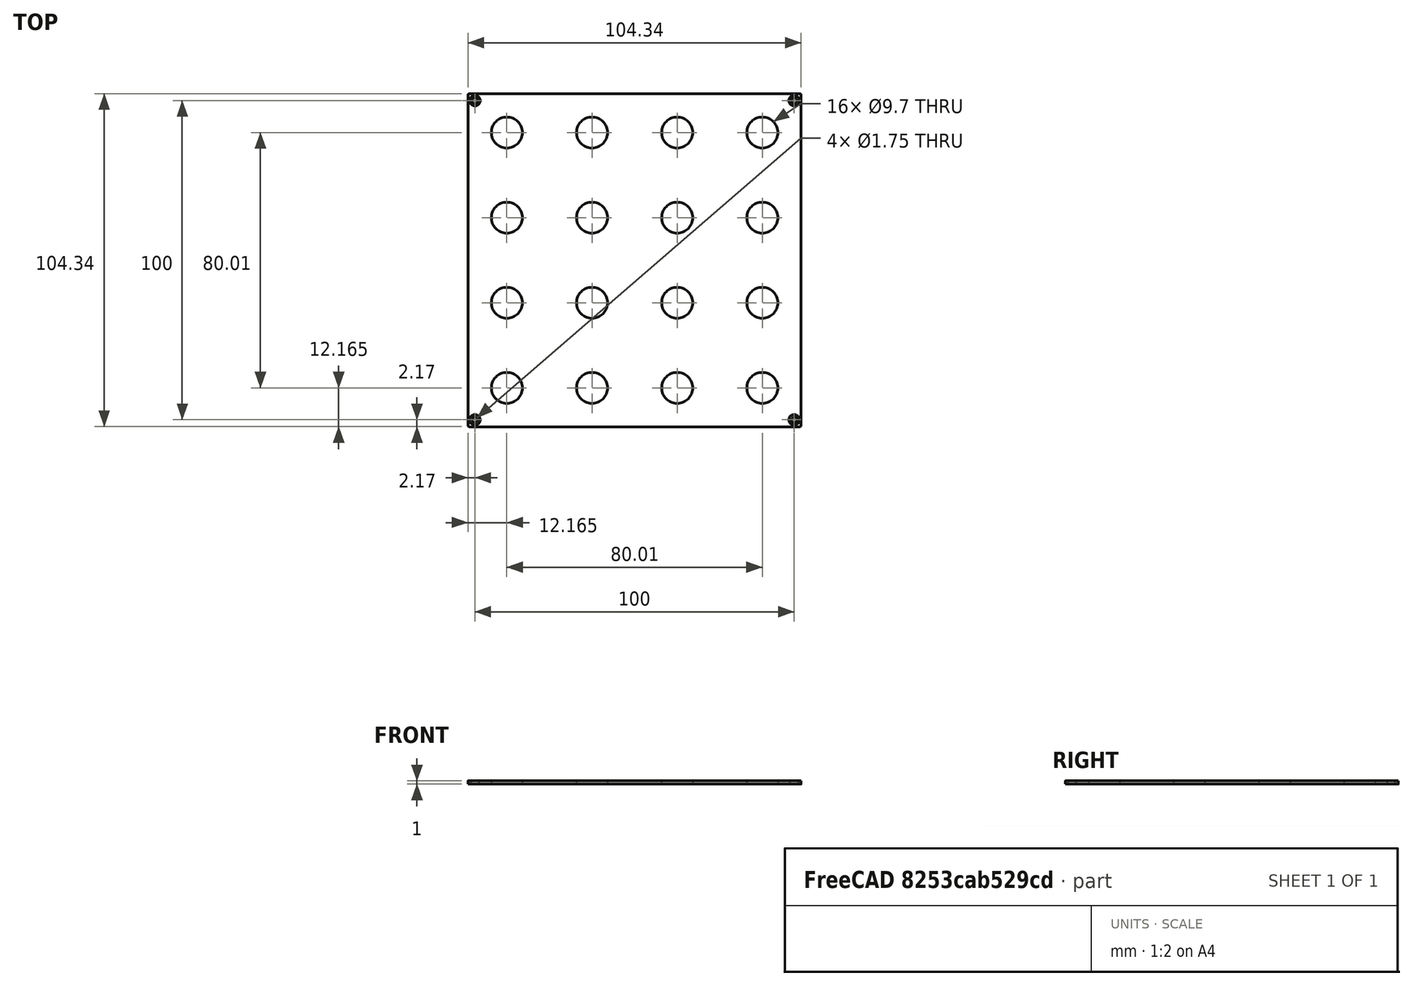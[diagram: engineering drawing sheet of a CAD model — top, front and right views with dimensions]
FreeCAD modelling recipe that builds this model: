
FCSTD DOCUMENT  (FreeCAD 0.21R33668 +26 (Git))
Label: FRONTPANEL-SHEET-BU16_wo_lightpipe
License: All rights reserved
LicenseURL: https://en.wikipedia.org/wiki/All_rights_reserved
objects: TechDraw::DrawViewBalloon×10, TechDraw::DrawViewDimension×8, Sketcher::SketchObject×6, TechDraw::DrawViewPart×5, TechDraw::DrawViewAnnotation×3, TechDraw::DrawSVGTemplate×2, PartDesign::Hole×2, PartDesign::Body×2, TechDraw::DrawPage×2, Spreadsheet::Sheet×1, PartDesign::Pad×1, PartDesign::Pocket×1, PartDesign::FeatureBase×1, TechDraw::DrawHatch×1, TechDraw::DrawComplexSection×1
note: 28 computed .brp shape members not serialized (recipe doc carries the construction recipe); baked Part::Feature solids carry a one-line shape summary decoded from their .brp

FEATURE [TechDraw::DrawSVGTemplate] Template003
  EditableTexts = COLOR=Anodized matte black - RAL code: 9004; CreationDate=2023/12/05; E.G.APPROVED=APPROVED; FC-Scale=1:1; FC-Title=BU16 - top cover; IntechStudioLtd.=Intech Studio Ltd.; MATERIAL=Aluminum 5052-H32; REV=02; STANDARD=ISO 2768 - m
  Height = 297
  Orientation = 1
  Template = <userpath>/Desktop/A3_LandscapeTD_MODIFIED.svg
  Width = 420
FEATURE [Spreadsheet::Sheet] Spreadsheet  label="dim"
  cells = A1='panel_length; B1(panel_length)=104.35; A2='panel_thickness; B2(panel_thickness)=1; A3='panel_radius; B3(panel_radius)==(104.35 - 103.6) / 2; A5='corner_drill_dist; B5(corner_drill_dist)=100; A6='corner_drill_dia; B6(corner_drill_dia)=1.75; A7='corner_drill_countersink; B7(corner_drill_countersink)=3.3; A9='undercut_width; B9(undercut_width)=1; A10='undercut_length; B10(undercut_length)=90; A11='undercut_offset; B11(undercut_offset)=1; A12='undercut_depth; B12(undercut_depth)=0.8; A14='ui_raster; B14(ui_raster)=26.67; A16='light_drill_dia; B16(light_drill_dia)=3; D16='old 2.9; A17='light_bore_dia; B17(light_bore_dia)=3.45; C17='check; D17='old 3.30; E17='DEPRICATED; A18='light_bore_depth; B18(light_bore_depth)=0.4; C18='check; D18='old 0.40; E18='DEPRICATED; A20='pot_drill_dia; B20(pot_drill_dia)=9.7; C20='check; D20='old 6.20; A21='pot_led_dist; B21(pot_led_dist)=8.5; B22=0; A23='but_drill_dia; B23(but_drill_dia)=9.7; A24='but_led_dist; B24(but_led_dist)=8.5; A26='fad_cutout_width; B26(fad_cutout_width)=2; C26='check; D26='old 1.50; A27='fad_cutout_length; B27(fad_cutout_length)=36; A28='fad_led_dist; B28(fad_led_dist)=25; A30='enc_drill_dia; B30(enc_drill_dia)=9.7; C30='check; D30='old 6.20; A31='enc_led_dist; B31(enc_led_dist)=8.5; A33='longfad_cutout_width; B33(longfad_cutout_width)=2; A34='longfad_cutout_length; B34(longfad_cutout_length)=66; A36='panel_chamfer; B36(panel_chamfer)=0.2; C36='UPDATE DRAWING
FEATURE [Sketcher::SketchObject] Sketch006
  FullyConstrained = true
  MapMode = 5
  Support = -> [XY_Plane002]
  expr: Constraints[4] = <<dim>>.ui_raster
  expr: Constraints[84] = <<dim>>.but_led_dist
  sketch-geometry (34):
    g0: Circle CenterX=-40.005 CenterY=48.505 CenterZ=0 NormalX=0 NormalY=0 NormalZ=1 AngleXU=0 Radius=2
    g1: Circle CenterX=-13.335 CenterY=48.505 CenterZ=0 NormalX=0 NormalY=0 NormalZ=1 AngleXU=0 Radius=2
    g2: LineSegment StartX=-40.005 StartY=48.505 StartZ=0 EndX=-13.335 EndY=48.505 EndZ=0
    g3: Circle CenterX=13.335 CenterY=48.505 CenterZ=0 NormalX=0 NormalY=0 NormalZ=1 AngleXU=0 Radius=2
    g4: LineSegment StartX=-13.335 StartY=48.505 StartZ=0 EndX=13.335 EndY=48.505 EndZ=0
    g5: Circle CenterX=40.005 CenterY=48.505 CenterZ=0 NormalX=0 NormalY=0 NormalZ=1 AngleXU=0 Radius=2
    g6: LineSegment StartX=13.335 StartY=48.505 StartZ=0 EndX=40.005 EndY=48.505 EndZ=0
    g7: Circle CenterX=-40.005 CenterY=21.835 CenterZ=0 NormalX=0 NormalY=0 NormalZ=1 AngleXU=0 Radius=2
    g8: LineSegment StartX=-40.005 StartY=48.505 StartZ=0 EndX=-40.005 EndY=21.835 EndZ=0
    g9: Circle CenterX=-13.335 CenterY=21.835 CenterZ=0 NormalX=0 NormalY=0 NormalZ=1 AngleXU=0 Radius=2
    g10: LineSegment StartX=-40.005 StartY=21.835 StartZ=0 EndX=-13.335 EndY=21.835 EndZ=0
    g11: Circle CenterX=13.335 CenterY=21.835 CenterZ=0 NormalX=0 NormalY=0 NormalZ=1 AngleXU=0 Radius=2
    g12: LineSegment StartX=-13.335 StartY=21.835 StartZ=0 EndX=13.335 EndY=21.835 EndZ=0
    g13: Circle CenterX=40.005 CenterY=21.835 CenterZ=0 NormalX=0 NormalY=0 NormalZ=1 AngleXU=0 Radius=2
    g14: LineSegment StartX=13.335 StartY=21.835 StartZ=0 EndX=40.005 EndY=21.835 EndZ=0
    g15: Circle CenterX=-40.005 CenterY=-4.835 CenterZ=0 NormalX=0 NormalY=0 NormalZ=1 AngleXU=0 Radius=2
    g16: LineSegment StartX=-40.005 StartY=21.835 StartZ=0 EndX=-40.005 EndY=-4.835 EndZ=0
    g17: Circle CenterX=-13.335 CenterY=-4.835 CenterZ=0 NormalX=0 NormalY=0 NormalZ=1 AngleXU=0 Radius=2
    g18: LineSegment StartX=-40.005 StartY=-4.835 StartZ=0 EndX=-13.335 EndY=-4.835 EndZ=0
    g19: Circle CenterX=13.335 CenterY=-4.835 CenterZ=0 NormalX=0 NormalY=0 NormalZ=1 AngleXU=0 Radius=2
    g20: LineSegment StartX=-13.335 StartY=-4.835 StartZ=0 EndX=13.335 EndY=-4.835 EndZ=0
    g21: Circle CenterX=40.005 CenterY=-4.835 CenterZ=0 NormalX=0 NormalY=0 NormalZ=1 AngleXU=0 Radius=2
    g22: LineSegment StartX=13.335 StartY=-4.835 StartZ=0 EndX=40.005 EndY=-4.835 EndZ=0
    g23: Circle CenterX=-40.005 CenterY=-31.505 CenterZ=0 NormalX=0 NormalY=0 NormalZ=1 AngleXU=0 Radius=2
    g24: LineSegment StartX=-40.005 StartY=-4.835 StartZ=0 EndX=-40.005 EndY=-31.505 EndZ=0
    g25: Circle CenterX=-13.335 CenterY=-31.505 CenterZ=0 NormalX=0 NormalY=0 NormalZ=1 AngleXU=0 Radius=2
    g26: LineSegment StartX=-40.005 StartY=-31.505 StartZ=0 EndX=-13.335 EndY=-31.505 EndZ=0
    g27: Circle CenterX=13.335 CenterY=-31.505 CenterZ=0 NormalX=0 NormalY=0 NormalZ=1 AngleXU=0 Radius=2
    g28: LineSegment StartX=-13.335 StartY=-31.505 StartZ=0 EndX=13.335 EndY=-31.505 EndZ=0
    g29: Circle CenterX=40.005 CenterY=-31.505 CenterZ=0 NormalX=0 NormalY=0 NormalZ=1 AngleXU=0 Radius=2
    g30: LineSegment StartX=13.335 StartY=-31.505 StartZ=0 EndX=40.005 EndY=-31.505 EndZ=0
    g31: LineSegment StartX=-13.335 StartY=21.835 StartZ=0 EndX=-1.8e-15 EndY=8.5 EndZ=0
    g32: LineSegment StartX=-1.8e-15 StartY=8.5 StartZ=0 EndX=13.335 EndY=21.835 EndZ=0
    g33: LineSegment StartX=-1.8e-15 StartY=8.5 StartZ=0 EndX=-13.335 EndY=-4.835 EndZ=0
  constraints (85):
    c: Diameter(g0) = 4
    c: Diameter(g1) = 4
    c: Coincident(g0,g2)
    c: Coincident(g1,g2)
    c: Distance(g2) = 26.67
    c: Angle(g2) = 0
    c: Diameter(g3) = 4
    c: Coincident(g1,g4)
    c: Coincident(g3,g4)
    c: Equal(g2,g4)
    c: Parallel(g4,g2)
    c: Diameter(g5) = 4
    c: Coincident(g3,g6)
    c: Coincident(g5,g6)
    c: Equal(g2,g6)
    c: Parallel(g6,g2)
    c: Diameter(g7) = 4
    c: Coincident(g0,g8)
    c: Coincident(g7,g8)
    c: Equal(g8,g2)
    c: Perpendicular(g8,g2)
    c: Diameter(g9) = 4
    c: Coincident(g7,g10)
    c: Coincident(g9,g10)
    c: Equal(g2,g10)
    c: Parallel(g10,g2)
    c: Diameter(g11) = 4
    c: Coincident(g9,g12)
    c: Coincident(g11,g12)
    c: Equal(g2,g12)
    c: Parallel(g12,g2)
    c: Diameter(g13) = 4
    c: Coincident(g11,g14)
    c: Coincident(g13,g14)
    c: Equal(g2,g14)
    c: Parallel(g14,g2)
    c: Diameter(g15) = 4
    c: Coincident(g7,g16)
    c: Coincident(g15,g16)
    c: Equal(g8,g16)
    c: Perpendicular(g16,g2)
    c: Diameter(g17) = 4
    c: Coincident(g15,g18)
    c: Coincident(g17,g18)
    c: Equal(g2,g18)
    c: Parallel(g18,g2)
    c: Diameter(g19) = 4
    c: Coincident(g17,g20)
    c: Coincident(g19,g20)
    c: Equal(g2,g20)
    c: Parallel(g20,g2)
    c: Diameter(g21) = 4
    c: Coincident(g19,g22)
    c: Coincident(g21,g22)
    c: Equal(g2,g22)
    c: Parallel(g22,g2)
    c: Diameter(g23) = 4
    c: Coincident(g15,g24)
    c: Coincident(g23,g24)
    c: Equal(g8,g24)
    c: Perpendicular(g24,g2)
    c: Diameter(g25) = 4
    c: Coincident(g23,g26)
    c: Coincident(g25,g26)
    c: Equal(g2,g26)
    c: Parallel(g26,g2)
    c: Diameter(g27) = 4
    c: Coincident(g25,g28)
    c: Coincident(g27,g28)
    c: Equal(g2,g28)
    c: Parallel(g28,g2)
    c: Diameter(g29) = 4
    c: Coincident(g27,g30)
    c: Coincident(g29,g30)
    c: Equal(g2,g30)
    c: Parallel(g30,g2)
    c: Coincident(g31,g9)
    c: PointOnObject(g31,g-2)
    c: Coincident(g31,g32)
    c: Coincident(g32,g11)
    c: Coincident(g31,g33)
    c: Coincident(g33,g17)
    c: Equal(g33,g31)
    c: Equal(g31,g32)
    c: DistanceY(g-1,g31) = 8.5
FEATURE [Sketcher::SketchObject] Sketch005
  FullyConstrained = true
  MapMode = 5
  Support = -> [XY_Plane002]
  expr: Constraints[4] = <<dim>>.ui_raster
  sketch-geometry (34):
    g0: Circle CenterX=-40.005 CenterY=40.005 CenterZ=0 NormalX=0 NormalY=0 NormalZ=1 AngleXU=0 Radius=2
    g1: Circle CenterX=-13.335 CenterY=40.005 CenterZ=0 NormalX=0 NormalY=0 NormalZ=1 AngleXU=0 Radius=2
    g2: LineSegment StartX=-40.005 StartY=40.005 StartZ=0 EndX=-13.335 EndY=40.005 EndZ=0
    g3: Circle CenterX=13.335 CenterY=40.005 CenterZ=0 NormalX=0 NormalY=0 NormalZ=1 AngleXU=0 Radius=2
    g4: LineSegment StartX=-13.335 StartY=40.005 StartZ=0 EndX=13.335 EndY=40.005 EndZ=0
    g5: Circle CenterX=40.005 CenterY=40.005 CenterZ=0 NormalX=0 NormalY=0 NormalZ=1 AngleXU=0 Radius=2
    g6: LineSegment StartX=13.335 StartY=40.005 StartZ=0 EndX=40.005 EndY=40.005 EndZ=0
    g7: Circle CenterX=-40.005 CenterY=13.335 CenterZ=0 NormalX=0 NormalY=0 NormalZ=1 AngleXU=0 Radius=2
    g8: LineSegment StartX=-40.005 StartY=40.005 StartZ=0 EndX=-40.005 EndY=13.335 EndZ=0
    g9: Circle CenterX=-13.335 CenterY=13.335 CenterZ=0 NormalX=0 NormalY=0 NormalZ=1 AngleXU=0 Radius=2
    g10: LineSegment StartX=-40.005 StartY=13.335 StartZ=0 EndX=-13.335 EndY=13.335 EndZ=0
    g11: Circle CenterX=13.335 CenterY=13.335 CenterZ=0 NormalX=0 NormalY=0 NormalZ=1 AngleXU=0 Radius=2
    g12: LineSegment StartX=-13.335 StartY=13.335 StartZ=0 EndX=13.335 EndY=13.335 EndZ=0
    g13: Circle CenterX=40.005 CenterY=13.335 CenterZ=0 NormalX=0 NormalY=0 NormalZ=1 AngleXU=0 Radius=2
    g14: LineSegment StartX=13.335 StartY=13.335 StartZ=0 EndX=40.005 EndY=13.335 EndZ=0
    g15: Circle CenterX=-40.005 CenterY=-13.335 CenterZ=0 NormalX=0 NormalY=0 NormalZ=1 AngleXU=0 Radius=2
    g16: LineSegment StartX=-40.005 StartY=13.335 StartZ=0 EndX=-40.005 EndY=-13.335 EndZ=0
    g17: Circle CenterX=-13.335 CenterY=-13.335 CenterZ=0 NormalX=0 NormalY=0 NormalZ=1 AngleXU=0 Radius=2
    g18: LineSegment StartX=-40.005 StartY=-13.335 StartZ=0 EndX=-13.335 EndY=-13.335 EndZ=0
    g19: Circle CenterX=13.335 CenterY=-13.335 CenterZ=0 NormalX=0 NormalY=0 NormalZ=1 AngleXU=0 Radius=2
    g20: LineSegment StartX=-13.335 StartY=-13.335 StartZ=0 EndX=13.335 EndY=-13.335 EndZ=0
    g21: Circle CenterX=40.005 CenterY=-13.335 CenterZ=0 NormalX=0 NormalY=0 NormalZ=1 AngleXU=0 Radius=2
    g22: LineSegment StartX=13.335 StartY=-13.335 StartZ=0 EndX=40.005 EndY=-13.335 EndZ=0
    g23: Circle CenterX=-40.005 CenterY=-40.005 CenterZ=0 NormalX=0 NormalY=0 NormalZ=1 AngleXU=0 Radius=2
    g24: LineSegment StartX=-40.005 StartY=-13.335 StartZ=0 EndX=-40.005 EndY=-40.005 EndZ=0
    g25: Circle CenterX=-13.335 CenterY=-40.005 CenterZ=0 NormalX=0 NormalY=0 NormalZ=1 AngleXU=0 Radius=2
    g26: LineSegment StartX=-40.005 StartY=-40.005 StartZ=0 EndX=-13.335 EndY=-40.005 EndZ=0
    g27: Circle CenterX=13.335 CenterY=-40.005 CenterZ=0 NormalX=0 NormalY=0 NormalZ=1 AngleXU=0 Radius=2
    g28: LineSegment StartX=-13.335 StartY=-40.005 StartZ=0 EndX=13.335 EndY=-40.005 EndZ=0
    g29: Circle CenterX=40.005 CenterY=-40.005 CenterZ=0 NormalX=0 NormalY=0 NormalZ=1 AngleXU=0 Radius=2
    g30: LineSegment StartX=13.335 StartY=-40.005 StartZ=0 EndX=40.005 EndY=-40.005 EndZ=0
    g31: LineSegment StartX=-13.335 StartY=13.335 StartZ=0 EndX=-1.8e-15 EndY=0 EndZ=0
    g32: LineSegment StartX=-1.8e-15 StartY=0 StartZ=0 EndX=13.335 EndY=13.335 EndZ=0
    g33: LineSegment StartX=0 StartY=0 StartZ=0 EndX=-13.335 EndY=-13.335 EndZ=0
  constraints (84):
    c: Diameter(g0) = 4
    c: Diameter(g1) = 4
    c: Coincident(g0,g2)
    c: Coincident(g1,g2)
    c: Distance(g2) = 26.67
    c: Angle(g2) = 0
    c: Diameter(g3) = 4
    c: Coincident(g1,g4)
    c: Coincident(g3,g4)
    c: Equal(g2,g4)
    c: Parallel(g4,g2)
    c: Diameter(g5) = 4
    c: Coincident(g3,g6)
    c: Coincident(g5,g6)
    c: Equal(g2,g6)
    c: Parallel(g6,g2)
    c: Diameter(g7) = 4
    c: Coincident(g0,g8)
    c: Coincident(g7,g8)
    c: Equal(g8,g2)
    c: Perpendicular(g8,g2)
    c: Diameter(g9) = 4
    c: Coincident(g7,g10)
    c: Coincident(g9,g10)
    c: Equal(g2,g10)
    c: Parallel(g10,g2)
    c: Diameter(g11) = 4
    c: Coincident(g9,g12)
    c: Coincident(g11,g12)
    c: Equal(g2,g12)
    c: Parallel(g12,g2)
    c: Diameter(g13) = 4
    c: Coincident(g11,g14)
    c: Coincident(g13,g14)
    c: Equal(g2,g14)
    c: Parallel(g14,g2)
    c: Diameter(g15) = 4
    c: Coincident(g7,g16)
    c: Coincident(g15,g16)
    c: Equal(g8,g16)
    c: Perpendicular(g16,g2)
    c: Diameter(g17) = 4
    c: Coincident(g15,g18)
    c: Coincident(g17,g18)
    c: Equal(g2,g18)
    c: Parallel(g18,g2)
    c: Diameter(g19) = 4
    c: Coincident(g17,g20)
    c: Coincident(g19,g20)
    c: Equal(g2,g20)
    c: Parallel(g20,g2)
    c: Diameter(g21) = 4
    c: Coincident(g19,g22)
    c: Coincident(g21,g22)
    c: Equal(g2,g22)
    c: Parallel(g22,g2)
    c: Diameter(g23) = 4
    c: Coincident(g15,g24)
    c: Coincident(g23,g24)
    c: Equal(g8,g24)
    c: Perpendicular(g24,g2)
    c: Diameter(g25) = 4
    c: Coincident(g23,g26)
    c: Coincident(g25,g26)
    c: Equal(g2,g26)
    c: Parallel(g26,g2)
    c: Diameter(g27) = 4
    c: Coincident(g25,g28)
    c: Coincident(g27,g28)
    c: Equal(g2,g28)
    c: Parallel(g28,g2)
    c: Diameter(g29) = 4
    c: Coincident(g27,g30)
    c: Coincident(g29,g30)
    c: Equal(g2,g30)
    c: Parallel(g30,g2)
    c: Coincident(g31,g9)
    c: Coincident(g31,g-1)
    c: Coincident(g31,g32)
    c: Coincident(g32,g11)
    c: Coincident(g-1,g33)
    c: Coincident(g33,g17)
    c: Equal(g33,g31)
    c: Equal(g31,g32)
FEATURE [Sketcher::SketchObject] Sketch001
  FullyConstrained = true
  MapMode = 5
  Support = -> [XY_Plane]
  expr: Constraints[13] = <<dim>>.corner_drill_dist
  sketch-geometry (9):
    g0: LineSegment StartX=-50 StartY=50 StartZ=0 EndX=-50 EndY=-50 EndZ=0
    g1: LineSegment StartX=-50 StartY=-50 StartZ=0 EndX=50 EndY=-50 EndZ=0
    g2: LineSegment StartX=50 StartY=-50 StartZ=0 EndX=50 EndY=50 EndZ=0
    g3: LineSegment StartX=50 StartY=50 StartZ=0 EndX=-50 EndY=50 EndZ=0
    g4: Circle CenterX=0 CenterY=0 CenterZ=0 NormalX=0 NormalY=0 NormalZ=1 AngleXU=0 Radius=70.7107
    g5: Circle CenterX=-50 CenterY=50 CenterZ=0 NormalX=0 NormalY=0 NormalZ=1 AngleXU=0 Radius=0.5
    g6: Circle CenterX=50 CenterY=50 CenterZ=0 NormalX=0 NormalY=0 NormalZ=1 AngleXU=0 Radius=0.5
    g7: Circle CenterX=50 CenterY=-50 CenterZ=0 NormalX=0 NormalY=0 NormalZ=1 AngleXU=0 Radius=0.5
    g8: Circle CenterX=-50 CenterY=-50 CenterZ=0 NormalX=0 NormalY=0 NormalZ=1 AngleXU=0 Radius=0.5
  constraints (22):
    c: Coincident(g0,g1)
    c: Coincident(g1,g2)
    c: Coincident(g2,g3)
    c: Coincident(g3,g0)
    c: Equal(g0,g1)
    c: Equal(g0,g2)
    c: Equal(g0,g3)
    c: PointOnObject(g0,g4)
    c: PointOnObject(g1,g4)
    c: PointOnObject(g2,g4)
    c: PointOnObject(g3,g4)
    c: Coincident(g4,g-1)
    c: Horizontal(g3)
    c: DistanceX(g3,g3) = 100
    c: Coincident(g5,g0)
    c: Coincident(g6,g2)
    c: Coincident(g7,g1)
    c: Coincident(g8,g0)
    c: Diameter(g8) = 1
    c: Equal(g8,g7)
    c: Equal(g8,g6)
    c: Equal(g8,g5)
FEATURE [Sketcher::SketchObject] Sketch002
  AttachmentOffset = pos=(0,0,-4.8) rot=(0,0,1;0rad)
  FullyConstrained = true
  MapMode = 5
  Placement = pos=(0,0,-4.8) rot=(0,0,1;0rad)
  Support = -> [XY_Plane]
  expr: .AttachmentOffset.Base.z = -<<dim>>.undercut_depth - 4
  expr: Constraints[91] = <<dim>>.undercut_length
  expr: Constraints[92] = <<dim>>.undercut_width
  expr: Constraints[93] = <<dim>>.panel_length / 2 - <<dim>>.undercut_offset - <<dim>>.undercut_width / 2
  sketch-geometry (40):
    g0: LineSegment StartX=-45 StartY=50.175 StartZ=0 EndX=45 EndY=50.175 EndZ=0
    g1: LineSegment StartX=-45 StartY=51.175 StartZ=0 EndX=45 EndY=51.175 EndZ=0
    g2: LineSegment StartX=-50.675 StartY=45 StartZ=0 EndX=0 EndY=0 EndZ=0
    g3: LineSegment StartX=0 StartY=0 StartZ=0 EndX=-50.675 EndY=-45 EndZ=0
    g4: LineSegment StartX=0 StartY=0 StartZ=0 EndX=-45 EndY=50.675 EndZ=0
    g5: LineSegment StartX=45 StartY=50.675 StartZ=0 EndX=0 EndY=0 EndZ=0
    g6: LineSegment StartX=0 StartY=0 StartZ=0 EndX=50.675 EndY=45 EndZ=0
    g7: LineSegment StartX=50.675 StartY=-45 StartZ=0 EndX=0 EndY=0 EndZ=0
    g8: LineSegment StartX=0 StartY=0 StartZ=0 EndX=45 EndY=-50.675 EndZ=0
    g9: LineSegment StartX=0 StartY=0 StartZ=0 EndX=-45 EndY=-50.675 EndZ=0
    g10: ArcOfCircle CenterX=45 CenterY=50.675 CenterZ=0 NormalX=0 NormalY=0 NormalZ=1 AngleXU=0 Radius=0.5 StartAngle=4.71239 EndAngle=6.28319
    g11: ArcOfCircle CenterX=45 CenterY=50.675 CenterZ=0 NormalX=0 NormalY=0 NormalZ=1 AngleXU=0 Radius=0.5 StartAngle=0 EndAngle=1.5708
    g12: LineSegment StartX=45 StartY=50.675 StartZ=0 EndX=45.5 EndY=50.675 EndZ=0
    g13: ArcOfCircle CenterX=-45 CenterY=50.675 CenterZ=0 NormalX=0 NormalY=0 NormalZ=1 AngleXU=0 Radius=0.5 StartAngle=3.14159 EndAngle=4.71239
    g14: ArcOfCircle CenterX=-45 CenterY=50.675 CenterZ=0 NormalX=0 NormalY=0 NormalZ=1 AngleXU=0 Radius=0.5 StartAngle=1.5708 EndAngle=3.14159
    g15: LineSegment StartX=-45.5 StartY=50.675 StartZ=0 EndX=-45 EndY=50.675 EndZ=0
    g16: LineSegment StartX=-45 StartY=-51.175 StartZ=0 EndX=45 EndY=-51.175 EndZ=0
    g17: LineSegment StartX=-45 StartY=-50.175 StartZ=0 EndX=45 EndY=-50.175 EndZ=0
    g18: ArcOfCircle CenterX=45 CenterY=-50.675 CenterZ=0 NormalX=0 NormalY=0 NormalZ=1 AngleXU=0 Radius=0.5 StartAngle=4.71239 EndAngle=6.28319
    g19: ArcOfCircle CenterX=45 CenterY=-50.675 CenterZ=0 NormalX=0 NormalY=0 NormalZ=1 AngleXU=0 Radius=0.5 StartAngle=0 EndAngle=1.5708
    g20: LineSegment StartX=45 StartY=-50.675 StartZ=0 EndX=45.5 EndY=-50.675 EndZ=0
    g21: ArcOfCircle CenterX=-45 CenterY=-50.675 CenterZ=0 NormalX=0 NormalY=0 NormalZ=1 AngleXU=0 Radius=0.5 StartAngle=3.14159 EndAngle=4.71239
    g22: ArcOfCircle CenterX=-45 CenterY=-50.675 CenterZ=0 NormalX=0 NormalY=0 NormalZ=1 AngleXU=0 Radius=0.5 StartAngle=1.5708 EndAngle=3.14159
    g23: LineSegment StartX=-45.5 StartY=-50.675 StartZ=0 EndX=-45 EndY=-50.675 EndZ=0
    g24: LineSegment StartX=51.175 StartY=-45 StartZ=0 EndX=51.175 EndY=45 EndZ=0
    g25: LineSegment StartX=50.175 StartY=-45 StartZ=0 EndX=50.175 EndY=45 EndZ=0
    g26: ArcOfCircle CenterX=50.675 CenterY=45 CenterZ=0 NormalX=0 NormalY=0 NormalZ=1 AngleXU=0 Radius=0.5 StartAngle=3.8e-15 EndAngle=1.5708
    g27: ArcOfCircle CenterX=50.675 CenterY=45 CenterZ=0 NormalX=0 NormalY=0 NormalZ=1 AngleXU=0 Radius=0.5 StartAngle=1.5708 EndAngle=3.14159
    g28: LineSegment StartX=50.675 StartY=45 StartZ=0 EndX=50.675 EndY=45.5 EndZ=0
    g29: ArcOfCircle CenterX=50.675 CenterY=-45 CenterZ=0 NormalX=0 NormalY=0 NormalZ=1 AngleXU=0 Radius=0.5 StartAngle=4.71239 EndAngle=6.28319
    g30: ArcOfCircle CenterX=50.675 CenterY=-45 CenterZ=0 NormalX=0 NormalY=0 NormalZ=1 AngleXU=0 Radius=0.5 StartAngle=3.14159 EndAngle=4.71239
    g31: LineSegment StartX=50.675 StartY=-45.5 StartZ=0 EndX=50.675 EndY=-45 EndZ=0
    g32: LineSegment StartX=-50.175 StartY=-45 StartZ=0 EndX=-50.175 EndY=45 EndZ=0
    g33: LineSegment StartX=-51.175 StartY=-45 StartZ=0 EndX=-51.175 EndY=45 EndZ=0
    g34: ArcOfCircle CenterX=-50.675 CenterY=45 CenterZ=0 NormalX=0 NormalY=0 NormalZ=1 AngleXU=0 Radius=0.5 StartAngle=1.4e-15 EndAngle=1.5708
    g35: ArcOfCircle CenterX=-50.675 CenterY=45 CenterZ=0 NormalX=0 NormalY=0 NormalZ=1 AngleXU=0 Radius=0.5 StartAngle=1.5708 EndAngle=3.14159
    g36: LineSegment StartX=-50.675 StartY=45 StartZ=0 EndX=-50.675 EndY=45.5 EndZ=0
    g37: ArcOfCircle CenterX=-50.675 CenterY=-45 CenterZ=0 NormalX=0 NormalY=0 NormalZ=1 AngleXU=0 Radius=0.5 StartAngle=4.71239 EndAngle=6.28319
    g38: ArcOfCircle CenterX=-50.675 CenterY=-45 CenterZ=0 NormalX=0 NormalY=0 NormalZ=1 AngleXU=0 Radius=0.5 StartAngle=3.14159 EndAngle=4.71239
    g39: LineSegment StartX=-50.675 StartY=-45.5 StartZ=0 EndX=-50.675 EndY=-45 EndZ=0
  constraints (96):
    c: Horizontal(g0)
    c: Coincident(g2,g-1)
    c: Coincident(g2,g3)
    c: Coincident(g-1,g4)
    c: Coincident(g5,g-1)
    c: Coincident(g5,g6)
    c: Coincident(g7,g-1)
    c: Coincident(g7,g8)
    c: Coincident(g-1,g9)
    c: Equal(g5,g6)
    c: Equal(g6,g8)
    c: Equal(g8,g7)
    c: Equal(g7,g9)
    c: Equal(g9,g3)
    c: Equal(g3,g2)
    c: Equal(g2,g4)
    c: Coincident(g10,g5)
    c: Coincident(g11,g10)
    c: Coincident(g11,g10)
    c: Tangent(g11,g1) = 1.5708
    c: Tangent(g10,g0) = -1.5708
    c: Coincident(g12,g10)
    c: Coincident(g12,g10)
    c: Horizontal(g12)
    c: Coincident(g13,g4)
    c: Coincident(g14,g13)
    c: Coincident(g14,g13)
    c: Tangent(g14,g1) = 1.5708
    c: Tangent(g13,g0) = -1.5708
    c: Coincident(g15,g13)
    c: Coincident(g15,g13)
    c: Horizontal(g15)
    c: Horizontal(g1)
    c: Horizontal(g16)
    c: Coincident(g19,g18)
    c: Coincident(g19,g18)
    c: Tangent(g19,g17) = 1.5708
    c: Tangent(g18,g16) = -1.5708
    c: Coincident(g20,g18)
    c: Coincident(g20,g18)
    c: Horizontal(g20)
    c: Coincident(g22,g21)
    c: Coincident(g22,g21)
    c: Tangent(g22,g17) = 1.5708
    c: Tangent(g21,g16) = -1.5708
    c: Coincident(g23,g21)
    c: Coincident(g23,g21)
    c: Horizontal(g23)
    c: Horizontal(g17)
    c: Coincident(g21,g9)
    c: Coincident(g8,g18)
    c: Equal(g22,g14)
    c: Equal(g17,g1)
    c: Coincident(g27,g26)
    c: Coincident(g27,g26)
    c: Tangent(g27,g25) = 1.5708
    c: Tangent(g26,g24) = -1.5708
    c: Coincident(g28,g26)
    c: Coincident(g28,g26)
    c: Coincident(g30,g29)
    c: Coincident(g30,g29)
    c: Tangent(g30,g25) = 1.5708
    c: Tangent(g29,g24) = -1.5708
    c: Coincident(g31,g29)
    c: Coincident(g31,g29)
    c: Vertical(g31)
    c: Vertical(g28)
    c: Vertical(g25)
    c: Vertical(g24)
    c: Coincident(g35,g34)
    c: Coincident(g35,g34)
    c: Tangent(g35,g33) = 1.5708
    c: Tangent(g34,g32) = -1.5708
    c: Coincident(g36,g34)
    c: Coincident(g36,g34)
    c: Coincident(g38,g37)
    c: Coincident(g38,g37)
    c: Tangent(g38,g33) = 1.5708
    c: Tangent(g37,g32) = -1.5708
    c: Coincident(g39,g37)
    c: Coincident(g39,g37)
    c: Vertical(g39)
    c: Vertical(g36)
    c: Vertical(g33)
    c: Vertical(g32)
    c: Coincident(g6,g26)
    c: Coincident(g7,g29)
    c: Equal(g25,g0)
    c: Equal(g11,g27)
    c: Equal(g1,g33)
    c: Equal(g35,g11)
    c: DistanceX(g13,g10) = 90
    c: Diameter(g13) = 1
    c: DistanceY(g-1,g13) = 50.675
    c: Coincident(g2,g34)
    c: Coincident(g3,g37)
FEATURE [Sketcher::SketchObject] Sketch
  FullyConstrained = true
  MapMode = 5
  Support = -> [XY_Plane]
  expr: Constraints[12] = <<dim>>.panel_radius
  expr: Constraints[16] = <<dim>>.panel_length
  sketch-geometry (11):
    g0: LineSegment StartX=-51.8 StartY=52.175 StartZ=0 EndX=51.8 EndY=52.175 EndZ=0
    g1: LineSegment StartX=52.175 StartY=51.8 StartZ=0 EndX=52.175 EndY=-51.8 EndZ=0
    g2: LineSegment StartX=51.8 StartY=-52.175 StartZ=0 EndX=-51.8 EndY=-52.175 EndZ=0
    g3: LineSegment StartX=-52.175 StartY=-51.8 StartZ=0 EndX=-52.175 EndY=51.8 EndZ=0
    g4: ArcOfCircle CenterX=-51.8 CenterY=51.8 CenterZ=0 NormalX=0 NormalY=0 NormalZ=1 AngleXU=0 Radius=0.375 StartAngle=1.5708 EndAngle=3.14159
    g5: ArcOfCircle CenterX=51.8 CenterY=51.8 CenterZ=0 NormalX=0 NormalY=0 NormalZ=1 AngleXU=0 Radius=0.375 StartAngle=8.4e-15 EndAngle=1.5708
    g6: ArcOfCircle CenterX=51.8 CenterY=-51.8 CenterZ=0 NormalX=0 NormalY=0 NormalZ=1 AngleXU=0 Radius=0.375 StartAngle=4.71239 EndAngle=6.28319
    g7: ArcOfCircle CenterX=-51.8 CenterY=-51.8 CenterZ=0 NormalX=0 NormalY=0 NormalZ=1 AngleXU=0 Radius=0.375 StartAngle=3.14159 EndAngle=4.71239
    g8: LineSegment StartX=-51.8 StartY=51.8 StartZ=0 EndX=0 EndY=0 EndZ=0
    g9: LineSegment StartX=0 StartY=0 StartZ=0 EndX=51.8 EndY=51.8 EndZ=0
    g10: LineSegment StartX=0 StartY=0 StartZ=0 EndX=-51.8 EndY=-51.8 EndZ=0
  constraints (26):
    c: Horizontal(g0)
    c: Horizontal(g2)
    c: Vertical(g1)
    c: Vertical(g3)
    c: Tangent(g3,g4) = 1.5708
    c: Tangent(g0,g4) = 1.5708
    c: Tangent(g0,g5) = 1.5708
    c: Tangent(g1,g5) = 1.5708
    c: Tangent(g1,g6) = 1.5708
    c: Tangent(g2,g6) = 1.5708
    c: Tangent(g2,g7) = 1.5708
    c: Tangent(g3,g7) = 1.5708
    c: Radius(g4) = 0.375
    c: Equal(g4,g5)
    c: Equal(g4,g6)
    c: Equal(g4,g7)
    c: DistanceX(g3,g1) = 104.35
    c: Equal(g3,g0)
    c: Coincident(g8,g4)
    c: Coincident(g8,g-1)
    c: Coincident(g8,g9)
    c: Coincident(g9,g5)
    c: Coincident(g-1,g10)
    c: Coincident(g10,g7)
    c: Equal(g10,g8)
    c: Equal(g8,g9)
FEATURE [PartDesign::Pad] Pad  label="panel"
  AllowMultiFace = false
  Direction = (0,0,1)
  Length = 1
  Length2 = 100
  Profile = -> Sketch
  Reversed = true
  Type = 0
  expr: Length = <<dim>>.panel_thickness
FEATURE [PartDesign::Pocket] Pocket
  AllowMultiFace = false
  BaseFeature = -> Pad
  Direction = (0,0,-1)
  Length = 5
  Length2 = 100
  Profile = -> Sketch002
  Type = 1
FEATURE [PartDesign::Hole] Hole
  BaseFeature = -> Pocket
  CustomThreadClearance = 0
  Depth = 298.105
  DepthType = 1
  Diameter = 1.75
  DrillForDepth = false
  DrillPoint = 1
  DrillPointAngle = 118
  HoleCutCountersinkAngle = 90
  HoleCutCustomValues = false
  HoleCutDepth = 0
  HoleCutDiameter = 3.3
  HoleCutType = 2
  ModelThread = false
  Profile = -> Sketch001
  Tapered = false
  TaperedAngle = 90
  ThreadClass = 0
  ThreadDepth = 298.105
  ThreadDepthType = 0
  ThreadDirection = 0
  ThreadFit = 0
  ThreadSize = 0
  ThreadType = 0
  Threaded = false
  UseCustomThreadClearance = false
  expr: Diameter = <<dim>>.corner_drill_dia
  expr: HoleCutDiameter = <<dim>>.corner_drill_countersink
FEATURE [PartDesign::Body] Body  label="Base"
  Group = -> [Sketch,Pad,Sketch001,Sketch002,Pocket,Hole]
  Origin = -> Origin
  Tip = -> Hole
FEATURE [PartDesign::FeatureBase] Clone001
  BaseFeature = -> Body
FEATURE [PartDesign::Hole] Hole003  label="BU16_ButtonHole"
  AllowMultiFace = false
  BaseFeature = -> Clone001
  CustomThreadClearance = 0
  Depth = 25
  DepthType = 1
  Diameter = 9.7
  DrillForDepth = false
  DrillPoint = 0
  DrillPointAngle = 118
  HoleCutCountersinkAngle = 90
  HoleCutCustomValues = false
  HoleCutDepth = 0
  HoleCutDiameter = 0
  HoleCutType = 0
  ModelThread = false
  Profile = -> Sketch005
  Tapered = false
  TaperedAngle = 90
  ThreadClass = 0
  ThreadDepth = 23.5
  ThreadDepthType = 0
  ThreadDirection = 0
  ThreadFit = 0
  ThreadSize = 0
  ThreadType = 0
  Threaded = false
  UseCustomThreadClearance = false
  expr: Diameter = <<dim>>.but_drill_dia
FEATURE [TechDraw::DrawViewAnnotation] Annotation
  Font = osifont
  LineSpace = 100
  LockPosition = false
  MaxWidth = -1
  Rotation = 0
  ScaleType = 0
  Text = 10:1
  TextSize = 4
  TextStyle = 0
  X = 79.1804
  Y = 41.3447
FEATURE [TechDraw::DrawViewAnnotation] Annotation001
  Font = osifont
  LineSpace = 100
  LockPosition = false
  MaxWidth = -1
  Rotation = 0
  ScaleType = 0
  Text = 1:2
  TextSize = 4
  TextStyle = 0
  X = 378.532
  Y = 111.543
FEATURE [Sketcher::SketchObject] Sketch007
  FullyConstrained = false
  MapMode = 5
  Support = -> [XY_Plane002]
  sketch-geometry (1):
    g0: LineSegment StartX=-53.5 StartY=-50 StartZ=0 EndX=-46.5 EndY=-50 EndZ=0
  constraints (2):
    c: Horizontal(g0)
    c: DistanceX(g0,g0) = 7
FEATURE [PartDesign::Body] Body002  label="FRONTPANEL-SHEET-BU16"
  BaseFeature = -> Body
  Group = -> [Clone001,Sketch005,Hole003,Sketch006,Sketch007]
  Origin = -> Origin002
  Tip = -> Hole003
FEATURE [TechDraw::DrawViewPart] View  label="View 1"
  CoarseView = false
  Direction = (0,0,1)
  Focus = 100
  HardHidden = false
  IsoCount = 0
  IsoHidden = false
  IsoVisible = false
  LockPosition = false
  Perspective = false
  Rotation = 0
  ScaleType = 2
  ScrubCount = 0
  SeamHidden = false
  SeamVisible = false
  SmoothHidden = false
  SmoothVisible = true
  Source = -> [Body002]
  X = 93.8022
  XDirection = (1,0,0)
  Y = 200.975
FEATURE [TechDraw::DrawViewPart] View002  label="View 2"
  CoarseView = false
  Direction = (-1,0,0)
  Focus = 100
  HardHidden = true
  IsoCount = 0
  IsoHidden = false
  IsoVisible = false
  LockPosition = false
  Perspective = false
  Rotation = 0
  ScaleType = 0
  ScrubCount = 0
  SeamHidden = false
  SeamVisible = false
  SmoothHidden = false
  SmoothVisible = true
  Source = -> [Body002]
  X = 198.715
  XDirection = (0,0,1)
  Y = 204.233
FEATURE [TechDraw::DrawViewPart] View003  label="View 3"
  CoarseView = false
  Direction = (-0.57735,-0.57735,0.57735)
  Focus = 100
  HardHidden = false
  IsoCount = 0
  IsoHidden = false
  IsoVisible = false
  LockPosition = false
  Perspective = false
  Rotation = 0
  Scale = 0.5
  ScaleType = 2
  ScrubCount = 0
  SeamHidden = false
  SeamVisible = false
  SmoothHidden = false
  SmoothVisible = true
  Source = -> [Body002]
  X = 381.079
  XDirection = (-0.707107,5.7735e-07,-0.707107)
  Y = 142.767
FEATURE [TechDraw::DrawViewBalloon] Balloon007
  BubbleShape = 6
  EndType = 6
  EndTypeScale = 1
  KinkLength = -0.1
  LockPosition = false
  OriginX = 0.520628
  OriginY = 38.9805
  Rotation = 0
  ScaleType = 0
  ShapeScale = 1
  SourceView = -> View002
  Text = A
  TextWrapLen = -1
  X = 13.2545
  Y = 38.9634
FEATURE [TechDraw::DrawViewBalloon] Balloon009
  BubbleShape = 6
  EndType = 0
  EndTypeScale = 1
  KinkLength = -0.1
  LockPosition = false
  OriginX = 0.859808
  OriginY = -26.8614
  Rotation = 0
  ScaleType = 0
  ShapeScale = 1
  SourceView = -> View002
  Text = ⏥|0,2
  TextWrapLen = -1
  X = 24.6858
  Y = -26.8434
FEATURE [TechDraw::DrawViewBalloon] Balloon012
  BubbleShape = 6
  EndType = 6
  EndTypeScale = 1
  KinkLength = 0
  LockPosition = false
  OriginX = -18.185
  OriginY = -40.005
  Rotation = 0
  ScaleType = 0
  ShapeScale = 1
  SourceView = -> View
  Text = ⌖|⌀0,15|A|B|C
  TextWrapLen = -1
  X = 6.52725
  Y = -75.2914
FEATURE [TechDraw::DrawViewBalloon] Balloon013
  BubbleShape = 6
  EndType = 6
  EndTypeScale = 1
  KinkLength = 0
  LockPosition = false
  OriginX = -18.185
  OriginY = -40.005
  Rotation = 0
  ScaleType = 0
  ShapeScale = 1
  SourceView = -> View
  Text = ○|0,1
  TextWrapLen = -1
  X = -11.3647
  Y = -85.9016
FEATURE [TechDraw::DrawViewBalloon] Balloon016
  BubbleShape = 6
  EndType = 6
  EndTypeScale = 1
  KinkLength = 0
  LockPosition = false
  OriginX = 11.835
  OriginY = -31.505
  Rotation = 0
  ScaleType = 0
  ShapeScale = 1
  SourceView = -> View
  Text = ⌖|⌀0,15|A|B|C
  TextWrapLen = -1
  X = 116.475
  Y = -74.8851
FEATURE [TechDraw::DrawViewBalloon] Balloon018
  BubbleShape = 1
  EndType = 3
  EndTypeScale = 1
  KinkLength = -0.1
  LockPosition = false
  OriginX = 0.982541
  OriginY = -23.626
  Rotation = 0
  ScaleType = 0
  ShapeScale = 1
  SourceView = -> View003
  Text = Aesthetical surfaces colored red on 3D file\nNo scratches, burrs or any kind of damage allowed!
  TextWrapLen = -1
  X = -201.268
  Y = -91.1104
FEATURE [TechDraw::DrawViewDimension] Dimension
  AngleOverride = false
  Arbitrary = false
  ArbitraryTolerances = false
  EqualTolerance = true
  ExtensionAngle = 0
  FormatSpec = 16x ⌀%.2w
  FormatSpecOverTolerance = %+.2w
  FormatSpecUnderTolerance = %+.2w
  Inverted = false
  LineAngle = 0
  LockPosition = false
  MeasureType = 1
  OverTolerance = 0.05
  References2D = -> [View]
  Rotation = 0
  ScaleType = 0
  TheoreticalExact = false
  Type = 5
  UnderTolerance = -0.05
  X = 104.83
  Y = -64.0313
FEATURE [TechDraw::DrawHatch] Hatch  label="HatchF1"
  HatchPattern = C:/Program Files/FreeCAD 0.21/data/Mod/TechDraw/Patterns/solid.svg
  Source = -> View003 [Face1]
FEATURE [TechDraw::DrawViewDimension] Dimension010
  AngleOverride = false
  Arbitrary = false
  ArbitraryTolerances = false
  EqualTolerance = false
  ExtensionAngle = 0
  FormatSpec = %.2w
  FormatSpecOverTolerance = %+.2w
  FormatSpecUnderTolerance = %+.2w
  Inverted = false
  LineAngle = 0
  LockPosition = false
  MeasureType = 1
  OverTolerance = 0
  References2D = -> [View]
  Rotation = 0
  ScaleType = 0
  TheoreticalExact = false
  Type = 2
  UnderTolerance = -0.2
  X = 64.8724
  Y = 2.41468
FEATURE [TechDraw::DrawViewBalloon] Balloon
  BubbleShape = 6
  EndType = 6
  EndTypeScale = 1
  KinkLength = 0
  LockPosition = false
  OriginX = 73.5813
  OriginY = 52.2676
  Rotation = 0
  ScaleType = 0
  ShapeScale = 1
  SourceView = -> Dimension010
  Text = C
  TextWrapLen = -1
  X = 73.6486
  Y = 64.8567
FEATURE [TechDraw::DrawViewPart] View004
  CoarseView = false
  Direction = (0,0,-1)
  Focus = 100
  HardHidden = true
  IsoCount = 0
  IsoHidden = false
  IsoVisible = false
  LockPosition = false
  Perspective = false
  Rotation = 0
  ScaleType = 0
  ScrubCount = 0
  SeamHidden = false
  SeamVisible = true
  SmoothHidden = false
  SmoothVisible = true
  Source = -> [Body002]
  X = 297.303
  XDirection = (-1,-1e-06,0)
  Y = 200.441
FEATURE [TechDraw::DrawViewDimension] Dimension011
  AngleOverride = false
  Arbitrary = false
  ArbitraryTolerances = false
  EqualTolerance = false
  ExtensionAngle = 0
  FormatSpec = %.2w
  FormatSpecOverTolerance = %+.2w
  FormatSpecUnderTolerance = %+.2w
  Inverted = false
  LineAngle = 0
  LockPosition = false
  MeasureType = 1
  OverTolerance = 0
  References2D = -> [View004]
  Rotation = 0
  ScaleType = 0
  TheoreticalExact = false
  Type = 1
  UnderTolerance = -0.2
  X = -0.499889
  Y = 65.7969
FEATURE [TechDraw::DrawViewBalloon] Balloon022
  BubbleShape = 6
  EndType = 6
  EndTypeScale = 1
  KinkLength = -0.1
  LockPosition = false
  OriginX = -52.2651
  OriginY = 58.6802
  Rotation = 0
  ScaleType = 0
  ShapeScale = 1
  SourceView = -> Dimension011
  Text = B
  TextWrapLen = -1
  X = -62.1979
  Y = 58.6576
FEATURE [TechDraw::DrawViewDimension] Dimension013
  AngleOverride = false
  Arbitrary = false
  ArbitraryTolerances = false
  EqualTolerance = true
  ExtensionAngle = 0
  FormatSpec = 16x ⌀%.2w
  FormatSpecOverTolerance = %+.2w
  FormatSpecUnderTolerance = %+.2w
  Inverted = false
  LineAngle = 0
  LockPosition = false
  MeasureType = 1
  OverTolerance = 0
  References2D = -> [View]
  Rotation = 0
  ScaleType = 0
  TheoreticalExact = false
  Type = 5
  UnderTolerance = 0
  X = -11.2012
  Y = -64.4638
FEATURE [TechDraw::DrawComplexSection] ComplexSection  label="Section A - A"
  BaseView = -> View
  Caption = Section A-A
  CoarseView = false
  CutSurfaceDisplay = 2
  CuttingToolWireObject = -> Sketch007
  Direction = (1e-16,-1,0)
  FileGeomPattern = C:/Program Files/FreeCAD 0.21/data/Mod/TechDraw/PAT/FCPAT.pat
  FileHatchPattern = C:/Program Files/FreeCAD 0.21/data/Mod/TechDraw/Patterns/simple.svg
  Focus = 100
  FuseBeforeCut = false
  HardHidden = true
  HatchOffset = (0,0,0)
  HatchRotation = 0
  HatchScale = 1
  IsoCount = 0
  IsoHidden = false
  IsoVisible = false
  LockPosition = false
  NameGeomPattern = Gyémánt bevonatú
  Perspective = false
  ProjectionStrategy = 1
  Rotation = 0
  Scale = 10
  ScaleType = 2
  ScrubCount = 0
  SeamHidden = false
  SeamVisible = true
  SectionDirection = 4
  SectionNormal = (1e-16,-1,0)
  SectionOrigin = (0,0,0)
  SectionSymbol = A
  SmoothHidden = false
  SmoothVisible = true
  Source = -> [Body002]
  TrimAfterCut = false
  X = 79.5678
  XDirection = (1,1e-16,0)
  Y = 64.2074
FEATURE [TechDraw::DrawViewBalloon] Balloon023
  BubbleShape = 1
  EndType = 0
  EndTypeScale = 1
  KinkLength = -0.1
  LockPosition = false
  OriginX = -52.0652
  OriginY = 52.0652
  Rotation = 0
  ScaleType = 0
  ShapeScale = 1
  SourceView = -> View
  Text = 4x R0,38
  TextWrapLen = -1
  X = -70.0132
  Y = 68.6837
FEATURE [TechDraw::DrawViewDimension] Dimension014
  AngleOverride = false
  Arbitrary = false
  ArbitraryTolerances = false
  EqualTolerance = true
  ExtensionAngle = 0
  FormatSpec = %.2w
  FormatSpecOverTolerance = %+.2w
  FormatSpecUnderTolerance = %+.2w
  Inverted = false
  LineAngle = 0
  LockPosition = false
  MeasureType = 1
  OverTolerance = 0
  References2D = -> [ComplexSection]
  Rotation = 0
  ScaleType = 0
  TheoreticalExact = false
  Type = 6
  UnderTolerance = 0
  X = -27.7612
  Y = 28.1448
FEATURE [TechDraw::DrawViewDimension] Dimension015
  AngleOverride = false
  Arbitrary = false
  ArbitraryTolerances = false
  EqualTolerance = true
  ExtensionAngle = 0
  FormatSpec = 4x ⌀%.2w
  FormatSpecOverTolerance = %+.2w
  FormatSpecUnderTolerance = %+.2w
  Inverted = false
  LineAngle = 0
  LockPosition = false
  MeasureType = 1
  OverTolerance = 0
  References2D = -> [ComplexSection]
  Rotation = 0
  ScaleType = 0
  TheoreticalExact = false
  Type = 1
  UnderTolerance = 0
  X = 24.0105
  Y = 22.4679
FEATURE [TechDraw::DrawViewDimension] Dimension016
  AngleOverride = false
  Arbitrary = false
  ArbitraryTolerances = false
  EqualTolerance = true
  ExtensionAngle = 0
  FormatSpec = 4x ⌀%.2w
  FormatSpecOverTolerance = %+.2w
  FormatSpecUnderTolerance = %+.2w
  Inverted = false
  LineAngle = 0
  LockPosition = false
  MeasureType = 1
  OverTolerance = 0.05
  References2D = -> [ComplexSection]
  Rotation = 0
  ScaleType = 0
  TheoreticalExact = false
  Type = 1
  UnderTolerance = -0.05
  X = 52.1239
  Y = -3.38615
FEATURE [TechDraw::DrawViewDimension] Dimension017
  AngleOverride = false
  Arbitrary = false
  ArbitraryTolerances = false
  EqualTolerance = true
  ExtensionAngle = 0
  FormatSpec = (%.2w)
  FormatSpecOverTolerance = %+.2w
  FormatSpecUnderTolerance = %+.2w
  Inverted = false
  LineAngle = 0
  LockPosition = false
  MeasureType = 1
  OverTolerance = 0
  References2D = -> [ComplexSection]
  Rotation = 0
  ScaleType = 0
  TheoreticalExact = false
  Type = 2
  UnderTolerance = 0
  X = -38.4382
  Y = 1.69271
FEATURE [TechDraw::DrawViewBalloon] Balloon024
  BubbleShape = 6
  EndType = 6
  EndTypeScale = 1
  KinkLength = 0
  LockPosition = false
  OriginX = 48.1576
  OriginY = -16.4662
  Rotation = 0
  ScaleType = 0
  ShapeScale = 1
  SourceView = -> Dimension016
  Text = ⌖|⌀0,15|A|B|C
  TextWrapLen = -1
  X = 62.263
  Y = -14.1919
FEATURE [TechDraw::DrawViewAnnotation] Annotation002
  Font = osifont
  LineSpace = 100
  LockPosition = false
  MaxWidth = -1
  Rotation = 0
  ScaleType = 0
  Text = The mid of the datum plane A is preferred to be near to the lower limit of the | flatness tolerance zone. It can achieved with an additional bending step.
  TextSize = 4
  TextStyle = 0
  X = 313.098
  Y = 80.07
FEATURE [TechDraw::DrawPage] Page003  label="BU16_Drawing"
  KeepUpdated = true
  NextBalloonIndex = 32
  ProjectionType = 0
  Template = -> Template003
  Views = -> [View,View002,View003,Balloon007,Balloon009,Balloon012,Balloon013,Balloon016,Balloon018,Dimension,Dimension010,Balloon,View004,Dimension011,Balloon022,Annotation,Annotation001,Dimension013,ComplexSection,Balloon023,Dimension014,Dimension015,Dimension016,Dimension017,Balloon024,Annotation002]
FEATURE [TechDraw::DrawSVGTemplate] Template
  Height = 210
  Orientation = 1
  Template = C:/Program Files/FreeCAD 0.21/data/Mod/TechDraw/Templates/A4_Landscape_blank.svg
  Width = 297
FEATURE [TechDraw::DrawViewPart] View005
  CoarseView = false
  Direction = (0,0,1)
  Focus = 100
  HardHidden = false
  IsoCount = 0
  IsoHidden = false
  IsoVisible = true
  LockPosition = false
  Perspective = false
  Rotation = 0
  ScaleType = 0
  ScrubCount = 0
  SeamHidden = false
  SeamVisible = true
  SmoothHidden = false
  SmoothVisible = true
  Source = -> [Body002]
  X = 148.5
  XDirection = (1,0,0)
  Y = 105
FEATURE [TechDraw::DrawPage] Page  label="BU16_dxf"
  KeepUpdated = true
  NextBalloonIndex = 1
  ProjectionType = 0
  Template = -> Template
  Views = -> [View005]
